# Revit family: R-MTI-010
name_source: partatom
category: Portes
units: mm (PartAtom-declared; Revit-internal decimal feet)

## family parameters
Couper avec des vides une fois chargée = Non
Hôte = Mur
Partagée = Non
Point de calcul de pièce = Oui
Toujours verticalement = Non

## types (2) — shared parameters
1 Vantail = Oui
2 Vantaux = Non
A.E.V = A*2.E*4B.V*C3
Acoustique = Rw(C ; Ctr) = 32(-1;-1)
Certification = Marquage CE
Coloris_Chants = Peinture Laquée PMT - Gris Clair - RAL 7035
Coloris_Oculus = Peinture Laquée PMT - Gris Clair - RAL 7035
Coloris_Oculus Métal = Peinture Laquée PMT - Gris Clair - RAL 7035
Construction analytique = <Aucun>
Description = Bloc-porte métal issues de secours et de service MD 101 BSA 1 vantail, simple action, 32(-1; -1) dB, 1,8 W/m².K, A*2.E*4B.V*C3, conforme EN 14351-1 (CE système 3 ou 1 selon configuration), sur huisserie métal
Ep_Tôle_Profil = 2 mm  [stored 0.00656168 ft]
Epaisseurs_Vantaux = 57 mm  [stored 0.187008 ft]
Espacement_Paumelle_Vantail = 10 mm  [stored 0.0328084 ft]
Fabricant = MALERBA
Ferrage_Encastre = Non
Feuillure_Basse_Vantail = Non
Fiche_Produit = MTI-010
Hauteur Feuillure Basse Vantail = 15 mm  [stored 0.0492126 ft]
Hauteur_Axe_Bequille = 1045 mm  [stored 3.42848 ft]
Ht Microviseur = 1500 mm  [stored 4.92126 ft]
Huisserie_Bati_d'Angle = Non
Huisserie_HB_Banches = Non
Huisserie_HT_RV_Avec_contre_Feuillure = Non
Huisserie_HT_RV_Sans_contre_Feuillure = Oui
Huisserie_Reprise_de_Doublage = Non
Inv_Espacement_Paumelle_Vantail = 10 mm  [stored 0.0328084 ft]
Inv_Position_Largeur_Paumelle = 10 mm  [stored 0.0328084 ft]
Jeu_1 = 5 mm  [stored 0.0164042 ft]
Jeu_2 = 5 mm  [stored 0.0164042 ft]
Jeu_Côté_Articulation_Vantail = 4 mm  [stored 0.0131234 ft]
Jeu_Côté_Fermeture_Vantail = 2 mm  [stored 0.00656168 ft]
Jeu_Haut = 5 mm  [stored 0.0164042 ft]
Jeu_Traverse_Basse_Vantail = 8 mm  [stored 0.0262467 ft]
Jeu_Traverse_Haute_Vantail = 3 mm  [stored 0.00984252 ft]
Largeur Feuillure Battement Articulation = 15 mm  [stored 0.0492126 ft]
Largeur_Axe_Bequille = 50 mm  [stored 0.164042 ft]
Largeur_Contre_Feuillure_Profil = 25 mm  [stored 0.082021 ft]
Largeur_Feuillure_Battement_Semi_Fixe = 15 mm  [stored 0.0492126 ft]
Largeur_Feuillure_Battement_Service = 15 mm  [stored 0.0492126 ft]
Largeur_Feuillure_Profil = 25 mm  [stored 0.082021 ft]
Largeur_Parement_coté_Feuillure_Profil = 30 mm  [stored 0.0984252 ft]
Largeur_Parement_coté_opposé_Feuillure_Profil = 55 mm  [stored 0.180446 ft]
Largeur_Vantail_Semi_Fixe_Souhaitée = 430 mm  [stored 1.41076 ft]
Largeur_Vantail_Service_Souhaitée = 992 mm  [stored 3.25459 ft]
Materiau_Scellement = <Par catégorie>
Materiaux_Dominant = Métal
Microviseur = Non
Modèle = 48-SA-HM (2017)
Nombre_Vantaux = 1
Note d'identification = 1V - ACOUSTIQUE / AEV / THERMIQUE - BATTANTE NON FEU
Paumelle_4 = 165 mm
Position_Largeur_Paumelle = 4 mm  [stored 0.0131234 ft]
Profondeur Feuillure Basse Vantail = 25 mm  [stored 0.082021 ft]
Profondeur Feuillure Battement Articulation = 26 mm
Profondeur_Contre_Feuillure_Profil = 30 mm  [stored 0.0984252 ft]
Profondeur_Feuillure_Battement_Semi_Fixe = 14 mm  [stored 0.0459318 ft]
Profondeur_Feuillure_Battement_Service = 26 mm
Profondeur_Feuillure_Profil = 65 mm  [stored 0.213255 ft]
Profondeur_Retour_Parement_Profil = 18 mm  [stored 0.0590551 ft]
Profondeur_Totale_Pose_Tunnel_Profil = 115 mm
Reference_Commerciale = MD101BSA
Thermique (W/m2.°K) = 1.9
URL = https://www.malerba.fr
Visibilite_Paum-4 = Oui
Visibilite_Poignee = Oui
zero-valued in all types: --------- EQUIPEMENTS -----------------, Décalage_Largeur_Profil, Décalage_Profondeur_Profil, Décalage_Seuil_Vantail, Désaffleurement_Vantail, Jeu Profondeur Recouvrement Vantail, Largeur_Feuillure_hôte_coté_opposé, Largeur_Feuillure_hôte_coté_ouvrant, Paumelle_1, Profondeur_Feuillure_hôte_coté_opposé, Profondeur_Feuillure_hôte_coté_ouvrant, Reprise_Doublage_1, Reprise_Doublage_2, Reprise_Doublage_Haut

## per-type parameters (varying)
| type | Hauteur_Vantaux_Souhaitée | Paumelle_2 | Paumelle_3 |
| MTI-010 - 1 | 2054 mm  [stored 6.73885 ft] | 809 mm  [stored 2.6542 ft] | 809 mm  [stored 2.6542 ft] |
| MTI-010 - 2 | 2514 mm | 1059 mm | 1059 mm |

note: [stored X ft] marks values corroborated as IEEE doubles in the binary element streams (Revit-internal decimal feet)

## geometry (parser evidence)
native form markers: Blend x14
no freeform markers — native parametric forms only
